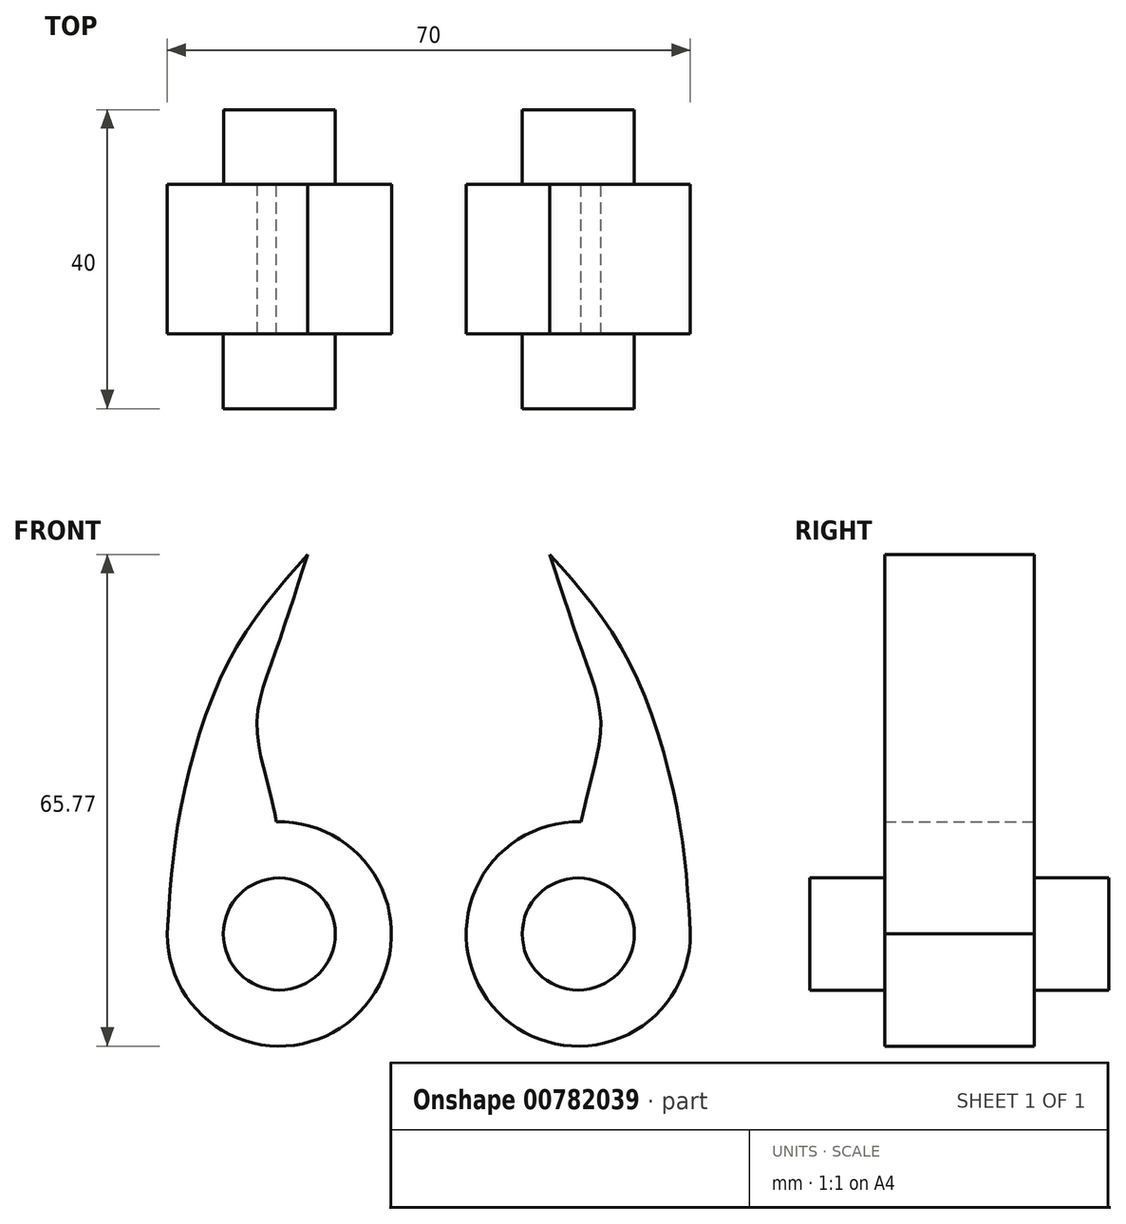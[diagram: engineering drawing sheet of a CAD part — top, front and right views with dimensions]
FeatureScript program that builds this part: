
annotation { "Feature Type Name" : "Feature", "Feature Type Description" : "" }
export const myFeature = defineFeature(function(context is Context, id is Id, definition is map)
    precondition{}
    {
        {
            var Q0;
            Q0=qCreatedBy(makeId("Front.planeOp"),FACE);
            var sketch = newSketch(context, id + "F0", { "sketchPlane" : qUnion([Q0])});
            skCircle(sketch, "E0", {"center": v(-40, 0) * mm, "radius": 15 * mm});
            skCircle(sketch, "E1", {"center": v(0, 0) * mm, "radius": 15 * mm});
            skFitSpline(sketch, "E2", {"points": [v(-55, 0) * mm, v(-53.37, 15.84) * mm, v(-46.56, 36.86) * mm, v(-36.2, 50.77) * mm], "startDerivative": vector(2.83, 48.48) * mm, "endDerivative": vector(34.45, 38.83) * mm});
            skFitSpline(sketch, "E3", {"points": [v(-36.2, 50.77) * mm, v(-40.64, 37.45) * mm, v(-43, 28.27) * mm, v(-41.53, 19.98) * mm, v(-40.38, 15) * mm], "startDerivative": vector(-14.43, -44.7) * mm, "endDerivative": vector(5.18, -24.64) * mm});
            skLineSegment(sketch, "E4", {"start": v(-20, -17.02) * mm, "end": v(-20, 46.98) * mm});
            skFitSpline(sketch, "E5.MirrorCS", {"points": [v(-3.8, 50.77) * mm, v(0.64, 37.45) * mm, v(3, 28.27) * mm, v(1.53, 19.98) * mm, v(0.38, 15) * mm], "startDerivative": vector(14.43, -44.7) * mm, "endDerivative": vector(-5.18, -24.64) * mm});
            skFitSpline(sketch, "E6.MirrorCS", {"points": [v(15, 0) * mm, v(13.37, 15.84) * mm, v(6.56, 36.86) * mm, v(-3.8, 50.77) * mm], "startDerivative": vector(-2.83, 48.48) * mm, "endDerivative": vector(-34.45, 38.83) * mm});
            skCircle(sketch, "E7", {"center": v(-40, 0) * mm, "radius": 7.5 * mm});
            skCircle(sketch, "E8", {"center": v(0, 0) * mm, "radius": 7.5 * mm});
            skSolve(sketch);
        }
        {
            var Q0;
            {var subQ0=sQuery(id+"F0.wireOp",EDGE,"E3");Q0=makeQuery(id+"F0.imprint","IMPRINT",FACE,{"disambiguationData":[TD([[makeQuery(id+"F0.imprint","IMPRINT",EDGE,{"derivedFrom":subQ0}),-1.0]])]});}
            var Q1;
            Q1=makeQuery(id+"F0.imprint","IMPRINT",FACE,{"disambiguationData":[TD([[makeQuery(id+"F0.imprint","IMPRINT",EDGE,{"derivedFrom":sQuery(id+"F0.wireOp",EDGE,"E7")}),-1.0]])]});
            var Q2;
            Q2=makeQuery(id+"F0.imprint","IMPRINT",FACE,{"disambiguationData":[TD([[makeQuery(id+"F0.imprint","IMPRINT",EDGE,{"derivedFrom":sQuery(id+"F0.wireOp",EDGE,"E8")}),-1.0]])]});
            var Q3;
            {var subQ0=sQuery(id+"F0.wireOp",EDGE,"E5.MirrorCS");Q3=makeQuery(id+"F0.imprint","IMPRINT",FACE,{"disambiguationData":[TD([[makeQuery(id+"F0.imprint","IMPRINT",EDGE,{"derivedFrom":subQ0}),1.0]])]});}
            extrude(context, id + "F1", {"entities" : qUnion([Q0, Q1, Q2, Q3]), "depth" : 20 * mm, "offsetDistance" : 25 * mm});
        }
        {
            var Q0;
            Q0=qCreatedBy(makeId("Front.planeOp"),FACE);
            var sketch = newSketch(context, id + "F2", { "sketchPlane" : qUnion([Q0])});
            skCircle(sketch, "E9", {"center": v(-40, 0) * mm, "radius": 7.46 * mm});
            skSolve(sketch);
        }
        {
            var Q0;
            Q0=makeQuery(id+"F0.imprint","IMPRINT",FACE,{"disambiguationData":[TD([[makeQuery(id+"F0.imprint","IMPRINT",EDGE,{"derivedFrom":sQuery(id+"F0.wireOp",EDGE,"E7")}),1.0]])]});
            extrude(context, id + "F3", {"entities" : qUnion([Q0]), "operationType" : NewBodyOperationType.ADD, "depth" : 30 * mm, "offsetDistance" : 25 * mm});
        }
        {
            var Q0;
            Q0=makeQuery(id+"F2.imprint","IMPRINT",FACE,{"disambiguationData":[TD([[makeQuery(id+"F2.imprint","IMPRINT",EDGE,{"derivedFrom":sQuery(id+"F2.wireOp",EDGE,"E9")}),1.0]])]});
            extrude(context, id + "F4", {"entities" : qUnion([Q0]), "operationType" : NewBodyOperationType.ADD, "depth" : 25 * mm, "offsetDistance" : 25 * mm, "hasSecondDirection" : true, "secondDirectionOppositeDirection" : true, "secondDirectionDepth" : 10 * mm});
        }
        {
            var Q0;
            Q0=makeQuery(id+"F0.imprint","IMPRINT",FACE,{"disambiguationData":[TD([[makeQuery(id+"F0.imprint","IMPRINT",EDGE,{"derivedFrom":sQuery(id+"F0.wireOp",EDGE,"E8")}),1.0]])]});
            extrude(context, id + "F5", {"entities" : qUnion([Q0]), "operationType" : NewBodyOperationType.ADD, "depth" : 30 * mm, "offsetDistance" : 25 * mm});
        }
        {
            var Q0;
            Q0=makeQuery(id+"F0.imprint","IMPRINT",FACE,{"disambiguationData":[TD([[makeQuery(id+"F0.imprint","IMPRINT",EDGE,{"derivedFrom":sQuery(id+"F0.wireOp",EDGE,"E8")}),1.0]])]});
            extrude(context, id + "F6", {"entities" : qUnion([Q0]), "operationType" : NewBodyOperationType.ADD, "depth" : 25 * mm, "offsetDistance" : 25 * mm, "hasSecondDirection" : true, "secondDirectionOppositeDirection" : true, "secondDirectionDepth" : 10 * mm});
        }
    });
